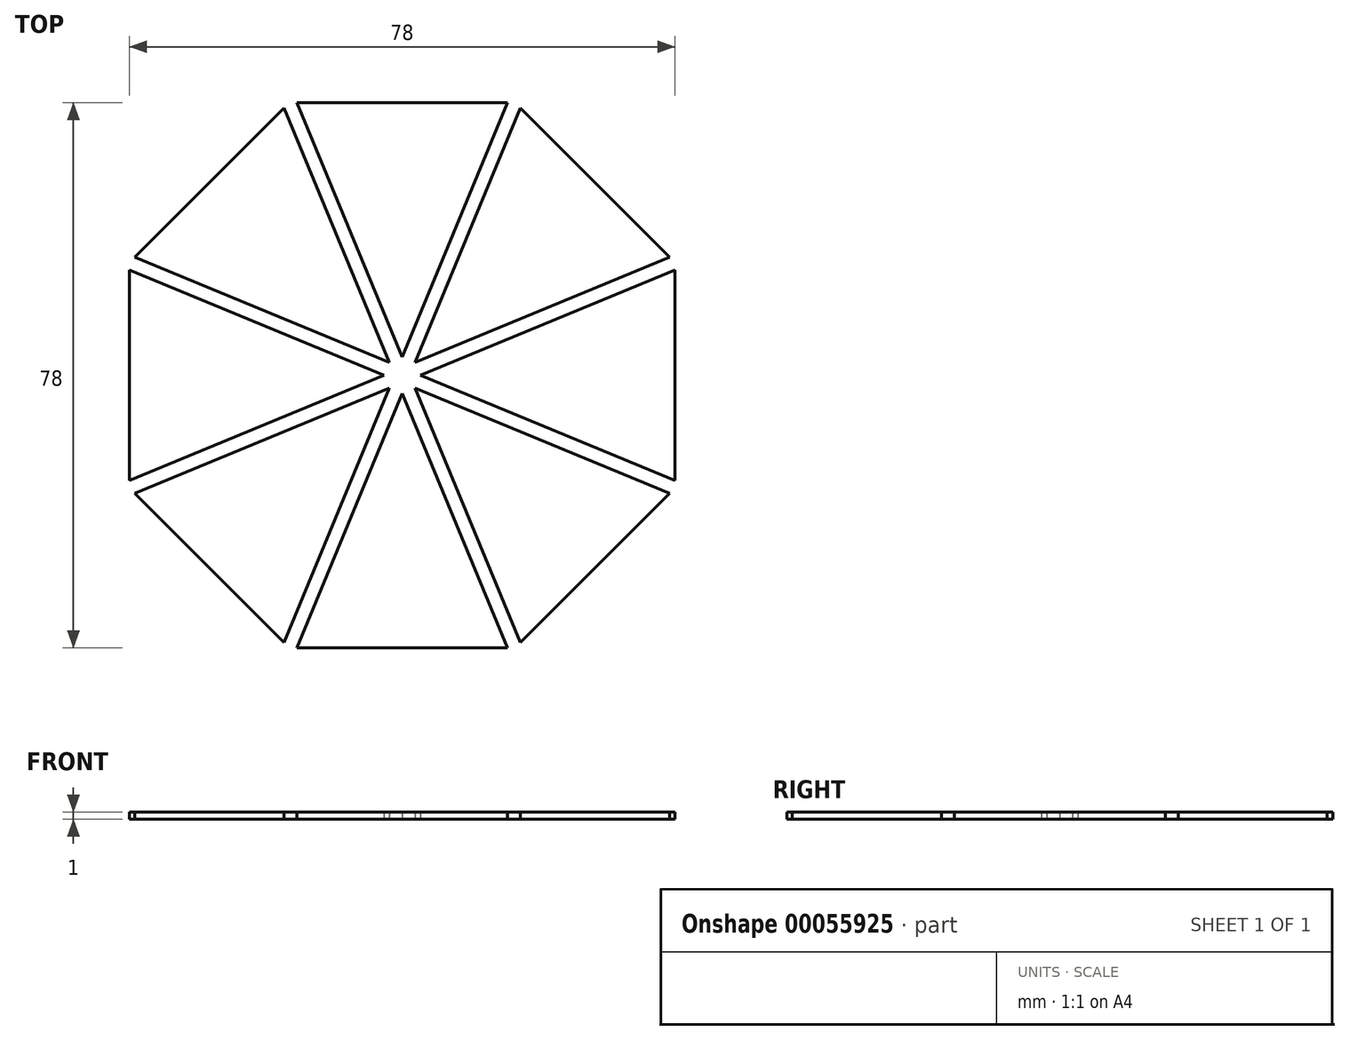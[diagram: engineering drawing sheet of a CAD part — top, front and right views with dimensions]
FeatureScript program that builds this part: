
annotation { "Feature Type Name" : "Feature", "Feature Type Description" : "" }
export const myFeature = defineFeature(function(context is Context, id is Id, definition is map)
    precondition{}
    {
        {
            var Q0;
            Q0=qCreatedBy(makeId("Top.planeOp"),FACE);
            var sketch = newSketch(context, id + "F0", { "sketchPlane" : qUnion([Q0])});
            skCircle(sketch, "E0.cCircle", {"center": v(0, 0) * mm, "radius": 40 * mm, "construction": true});
            skLineSegment(sketch, "E0.0", {"start": v(-16.57, 40) * mm, "end": v(16.57, 40) * mm, "construction": true});
            skLineSegment(sketch, "E0.1", {"start": v(16.57, 40) * mm, "end": v(40, 16.57) * mm, "construction": true});
            skLineSegment(sketch, "E0.2", {"start": v(40, 16.57) * mm, "end": v(40, -16.57) * mm, "construction": true});
            skLineSegment(sketch, "E0.3", {"start": v(40, -16.57) * mm, "end": v(16.57, -40) * mm, "construction": true});
            skLineSegment(sketch, "E0.4", {"start": v(16.57, -40) * mm, "end": v(-16.57, -40) * mm, "construction": true});
            skLineSegment(sketch, "E0.5", {"start": v(-16.57, -40) * mm, "end": v(-40, -16.57) * mm, "construction": true});
            skLineSegment(sketch, "E0.6", {"start": v(-40, -16.57) * mm, "end": v(-40, 16.57) * mm, "construction": true});
            skLineSegment(sketch, "E0.7", {"start": v(-40, 16.57) * mm, "end": v(-16.57, 40) * mm, "construction": true});
            skPoint(sketch, "E0.0.midPoint", {"position": v(0, 40) * mm});
            skLineSegment(sketch, "E1", {"start": v(-16.57, 40) * mm, "end": v(0, 0) * mm, "construction": true});
            skLineSegment(sketch, "E2", {"start": v(16.57, 40) * mm, "end": v(0, 0) * mm, "construction": true});
            skLineSegment(sketch, "E3.0", {"start": v(-15.07, 39) * mm, "end": v(0, 2.61) * mm});
            skLineSegment(sketch, "E3.1", {"start": v(-15.07, 39) * mm, "end": v(15.07, 39) * mm});
            skLineSegment(sketch, "E3.2", {"start": v(15.07, 39) * mm, "end": v(0, 2.61) * mm});
            skLineSegment(sketch, "E4.1.0", {"start": v(-38.23, 16.92) * mm, "end": v(-16.92, 38.23) * mm});
            skLineSegment(sketch, "E4.1.1", {"start": v(-16.92, 38.23) * mm, "end": v(-1.85, 1.85) * mm});
            skLineSegment(sketch, "E4.1.2", {"start": v(-38.23, 16.92) * mm, "end": v(-1.85, 1.85) * mm});
            skLineSegment(sketch, "E4.2.0", {"start": v(-39, -15.07) * mm, "end": v(-39, 15.07) * mm});
            skLineSegment(sketch, "E4.2.1", {"start": v(-39, 15.07) * mm, "end": v(-2.61, 0) * mm});
            skLineSegment(sketch, "E4.2.2", {"start": v(-39, -15.07) * mm, "end": v(-2.61, 0) * mm});
            skLineSegment(sketch, "E4.3.0", {"start": v(-16.92, -38.23) * mm, "end": v(-38.23, -16.92) * mm});
            skLineSegment(sketch, "E4.3.1", {"start": v(-38.23, -16.92) * mm, "end": v(-1.85, -1.85) * mm});
            skLineSegment(sketch, "E4.3.2", {"start": v(-16.92, -38.23) * mm, "end": v(-1.85, -1.85) * mm});
            skLineSegment(sketch, "E4.4.0", {"start": v(15.07, -39) * mm, "end": v(-15.07, -39) * mm});
            skLineSegment(sketch, "E4.4.1", {"start": v(-15.07, -39) * mm, "end": v(0, -2.61) * mm});
            skLineSegment(sketch, "E4.4.2", {"start": v(15.07, -39) * mm, "end": v(0, -2.61) * mm});
            skLineSegment(sketch, "E4.5.0", {"start": v(38.23, -16.92) * mm, "end": v(16.92, -38.23) * mm});
            skLineSegment(sketch, "E4.5.1", {"start": v(16.92, -38.23) * mm, "end": v(1.85, -1.85) * mm});
            skLineSegment(sketch, "E4.5.2", {"start": v(38.23, -16.92) * mm, "end": v(1.85, -1.85) * mm});
            skLineSegment(sketch, "E4.6.0", {"start": v(39, 15.07) * mm, "end": v(39, -15.07) * mm});
            skLineSegment(sketch, "E4.6.1", {"start": v(39, -15.07) * mm, "end": v(2.61, 0) * mm});
            skLineSegment(sketch, "E4.6.2", {"start": v(39, 15.07) * mm, "end": v(2.61, 0) * mm});
            skLineSegment(sketch, "E4.7.0", {"start": v(16.92, 38.23) * mm, "end": v(38.23, 16.92) * mm});
            skLineSegment(sketch, "E4.7.1", {"start": v(38.23, 16.92) * mm, "end": v(1.85, 1.85) * mm});
            skLineSegment(sketch, "E4.7.2", {"start": v(16.92, 38.23) * mm, "end": v(1.85, 1.85) * mm});
            skSolve(sketch);
        }
        {
            var Q0;
            Q0 = qSketchRegion(id + "F0", true);
            extrude(context, id + "F1", {"entities" : qUnion([Q0]), "depth" : 1 * mm});
        }
    });
